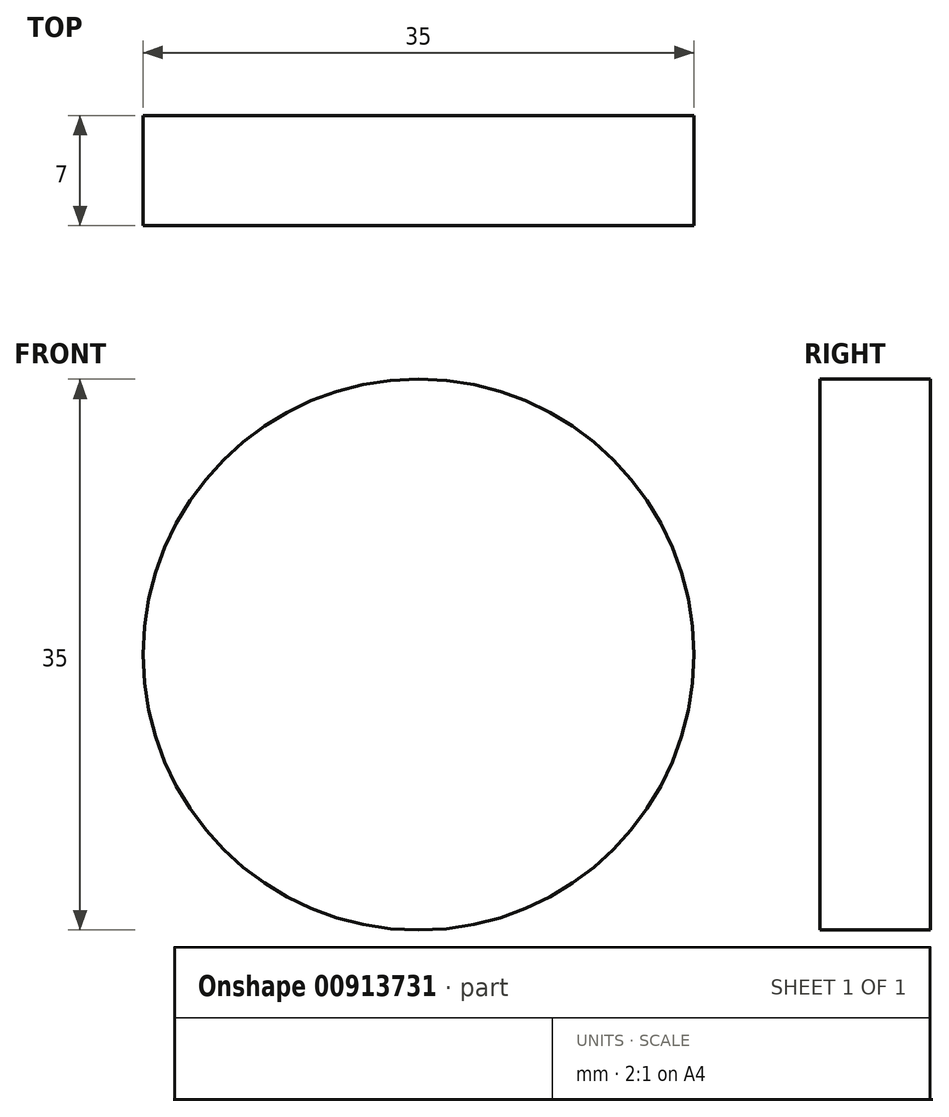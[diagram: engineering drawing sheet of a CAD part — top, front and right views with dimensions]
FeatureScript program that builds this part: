
annotation { "Feature Type Name" : "Feature", "Feature Type Description" : "" }
export const myFeature = defineFeature(function(context is Context, id is Id, definition is map)
    precondition{}
    {
        {
            var Q0;
            Q0=qCreatedBy(makeId("Front.planeOp"),FACE);
            var sketch = newSketch(context, id + "F0", { "sketchPlane" : qUnion([Q0])});
            skCircle(sketch, "E0", {"center": v(0, 0) * mm, "radius": 17.5 * mm});
            skSolve(sketch);
        }
        {
            var Q0;
            Q0 = qSketchRegion(id + "F0", true);
            extrude(context, id + "F1", {"entities" : qUnion([Q0]), "depth" : 7 * mm, "offsetDistance" : 25 * mm});
        }
    });
